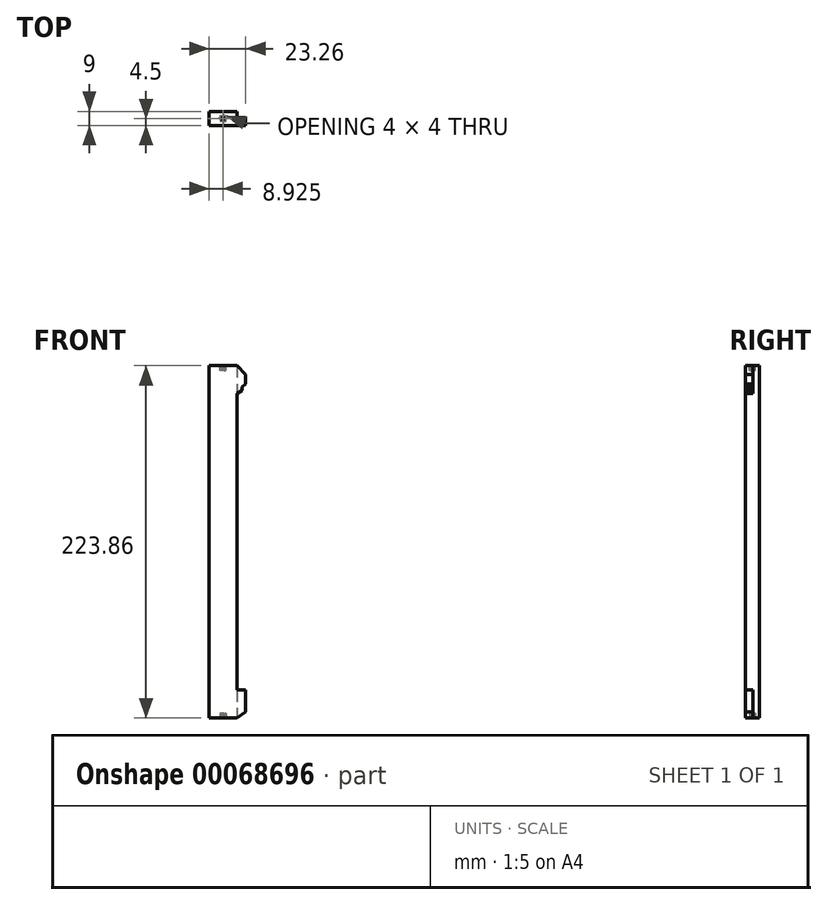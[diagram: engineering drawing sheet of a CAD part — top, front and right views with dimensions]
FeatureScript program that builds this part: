
annotation { "Feature Type Name" : "Feature", "Feature Type Description" : "" }
export const myFeature = defineFeature(function(context is Context, id is Id, definition is map)
    precondition{}
    {
        {
            var Q0;
            Q0=qCreatedBy(makeId("Front.planeOp"),FACE);
            var sketch = newSketch(context, id + "F0", { "sketchPlane" : qUnion([Q0])});
            skLineSegment(sketch, "E0", {"start": v(0, 111.93) * mm, "end": v(17.7, 111.93) * mm});
            skLineSegment(sketch, "E1", {"start": v(17.7, 111.93) * mm, "end": v(23.26, 106.39) * mm});
            skLineSegment(sketch, "E2", {"start": v(23.26, 106.39) * mm, "end": v(23.26, 100.4) * mm});
            skLineSegment(sketch, "E3", {"start": v(23.26, 100.4) * mm, "end": v(20.93, 98.25) * mm});
            skLineSegment(sketch, "E4", {"start": v(20.93, 98.25) * mm, "end": v(20.93, 96.18) * mm});
            skLineSegment(sketch, "E5", {"start": v(20.93, 96.18) * mm, "end": v(17.85, 94.28) * mm});
            skLineSegment(sketch, "E6", {"start": v(17.85, 94.28) * mm, "end": v(17.85, -94.03) * mm});
            skLineSegment(sketch, "E7", {"start": v(17.85, -94.03) * mm, "end": v(23.26, -94.03) * mm});
            skLineSegment(sketch, "E8", {"start": v(23.26, -94.03) * mm, "end": v(23.26, -107.9) * mm});
            skLineSegment(sketch, "E9", {"start": v(23.26, -107.9) * mm, "end": v(17.85, -111.93) * mm});
            skLineSegment(sketch, "E10", {"start": v(17.85, -111.93) * mm, "end": v(0, -111.93) * mm});
            skLineSegment(sketch, "E11", {"start": v(0, -111.93) * mm, "end": v(0, 111.93) * mm});
            skSolve(sketch);
        }
        {
            var Q0;
            Q0 = qSketchRegion(id + "F0", true);
            extrude(context, id + "F1", {"entities" : qUnion([Q0]), "depth" : 5 * mm});
        }
        {
            var Q0;
            Q0=makeQuery(id+"F1.opExtrude","CAP_FACE",FACE,{"disambiguationData":[OSD([sQuery(id+"F0.wireOp",EDGE,"E0"),sQuery(id+"F0.wireOp",EDGE,"E1"),sQuery(id+"F0.wireOp",EDGE,"E2"),sQuery(id+"F0.wireOp",EDGE,"E3"),sQuery(id+"F0.wireOp",EDGE,"E4"),sQuery(id+"F0.wireOp",EDGE,"E5"),sQuery(id+"F0.wireOp",EDGE,"E6"),sQuery(id+"F0.wireOp",EDGE,"E7"),sQuery(id+"F0.wireOp",EDGE,"E8"),sQuery(id+"F0.wireOp",EDGE,"E9"),sQuery(id+"F0.wireOp",EDGE,"E10"),sQuery(id+"F0.wireOp",EDGE,"E11")])],"isStart":true});
            var sketch = newSketch(context, id + "F2", { "sketchPlane" : qUnion([Q0])});
            skLineSegment(sketch, "E12.bottom", {"start": v(0, 111.93) * mm, "end": v(-17.85, 111.93) * mm});
            skLineSegment(sketch, "E12.top", {"start": v(0, -111.93) * mm, "end": v(-17.85, -111.93) * mm});
            skLineSegment(sketch, "E12.left", {"start": v(0, 111.93) * mm, "end": v(0, -111.93) * mm});
            skLineSegment(sketch, "E12.right", {"start": v(-17.85, 111.93) * mm, "end": v(-17.85, -111.93) * mm});
            skSolve(sketch);
        }
        {
            var Q0;
            Q0 = qSketchRegion(id + "F2", true);
            extrude(context, id + "F3", {"entities" : qUnion([Q0]), "operationType" : NewBodyOperationType.ADD, "depth" : 4 * mm});
        }
        {
            var Q0;
            Q0=makeQuery(id+"F3.boolean.opBoolean","MERGE",FACE,{"derivedFrom":[makeQuery(id+"F1.opExtrude","SWEPT_FACE",FACE,{"disambiguationData":[OSD([sQuery(id+"F0.wireOp",EDGE,"E0")])]}),makeQuery(id+"F3.opExtrude","SWEPT_FACE",FACE,{"disambiguationData":[OSD([sQuery(id+"F2.wireOp",EDGE,"E12.bottom")])]})]});
            var sketch = newSketch(context, id + "F4", { "sketchPlane" : qUnion([Q0])});
            skArc(sketch, "E13", {"start": v(7.51, -1) * mm, "mid": v(7.86, -1.56) * mm, "end": v(8.43, -1.91) * mm});
            skLineSegment(sketch, "E14.rect.bottom", {"start": v(10.93, 0) * mm, "end": v(10.34, 0) * mm});
            skLineSegment(sketch, "E14.rect.top", {"start": v(10.93, -1) * mm, "end": v(10.34, -1) * mm});
            skLineSegment(sketch, "E14.rect.left", {"start": v(10.93, 0) * mm, "end": v(10.93, -1) * mm});
            skLineSegment(sketch, "E14.rect.right", {"start": v(6.93, 0) * mm, "end": v(6.93, -1) * mm});
            skLineSegment(sketch, "E15.rect.bottom", {"start": v(9.43, 1.5) * mm, "end": v(8.43, 1.5) * mm});
            skLineSegment(sketch, "E15.rect.top", {"start": v(9.43, -2.5) * mm, "end": v(8.43, -2.5) * mm});
            skLineSegment(sketch, "E15.rect.left", {"start": v(9.43, 1.5) * mm, "end": v(9.43, 0.91) * mm});
            skLineSegment(sketch, "E15.rect.right", {"start": v(8.43, 1.5) * mm, "end": v(8.43, 0.91) * mm});
            skLineSegment(sketch, "E16.trimOffspring", {"start": v(7.51, 0) * mm, "end": v(6.93, 0) * mm});
            skLineSegment(sketch, "E17.trimOffspring", {"start": v(7.51, -1) * mm, "end": v(6.93, -1) * mm});
            skLineSegment(sketch, "E18.trimOffspring", {"start": v(8.43, -1.91) * mm, "end": v(8.43, -2.5) * mm});
            skLineSegment(sketch, "E19.trimOffspring", {"start": v(9.43, -1.91) * mm, "end": v(9.43, -2.5) * mm});
            skArc(sketch, "E20.trimOffspring", {"start": v(9.43, -1.91) * mm, "mid": v(9.99, -1.56) * mm, "end": v(10.34, -1) * mm});
            skArc(sketch, "E21.trimOffspring", {"start": v(10.34, 0) * mm, "mid": v(9.99, 0.56) * mm, "end": v(9.43, 0.91) * mm});
            skArc(sketch, "E22.trimOffspring", {"start": v(8.43, 0.91) * mm, "mid": v(7.86, 0.56) * mm, "end": v(7.51, 0) * mm});
            skSolve(sketch);
        }
        {
            var Q0;
            Q0 = qSketchRegion(id + "F4", true);
            extrude(context, id + "F5", {"entities" : qUnion([Q0]), "oppositeDirection" : true, "depth" : 3 * mm});
        }
        {
            var Q0;
            Q0=makeQuery(id+"F5.opExtrude","SWEPT_BODY",BODY,{"disambiguationData":[OSD([sQuery(id+"F4.wireOp",EDGE,"E13"),sQuery(id+"F4.wireOp",EDGE,"E14.rect.bottom"),sQuery(id+"F4.wireOp",EDGE,"E14.rect.top"),sQuery(id+"F4.wireOp",EDGE,"E14.rect.left"),sQuery(id+"F4.wireOp",EDGE,"E14.rect.right"),sQuery(id+"F4.wireOp",EDGE,"E15.rect.bottom"),sQuery(id+"F4.wireOp",EDGE,"E15.rect.top"),sQuery(id+"F4.wireOp",EDGE,"E15.rect.left"),sQuery(id+"F4.wireOp",EDGE,"E15.rect.right"),sQuery(id+"F4.wireOp",EDGE,"E16.trimOffspring"),sQuery(id+"F4.wireOp",EDGE,"E17.trimOffspring"),sQuery(id+"F4.wireOp",EDGE,"E18.trimOffspring"),sQuery(id+"F4.wireOp",EDGE,"E19.trimOffspring"),sQuery(id+"F4.wireOp",EDGE,"E20.trimOffspring"),sQuery(id+"F4.wireOp",EDGE,"E21.trimOffspring"),sQuery(id+"F4.wireOp",EDGE,"E22.trimOffspring")])]});
            var Q1;
            Q1=qCreatedBy(makeId("Top.planeOp"),FACE);
            mirror(context, id + "F6", {"entities" : qUnion([Q0]), "mirrorPlane" : qUnion([Q1])});
        }
        {
            var Q0;
            Q0=makeQuery(id+"F5.opExtrude","SWEPT_BODY",BODY,{"disambiguationData":[OSD([sQuery(id+"F4.wireOp",EDGE,"E13"),sQuery(id+"F4.wireOp",EDGE,"E14.rect.bottom"),sQuery(id+"F4.wireOp",EDGE,"E14.rect.top"),sQuery(id+"F4.wireOp",EDGE,"E14.rect.left"),sQuery(id+"F4.wireOp",EDGE,"E14.rect.right"),sQuery(id+"F4.wireOp",EDGE,"E15.rect.bottom"),sQuery(id+"F4.wireOp",EDGE,"E15.rect.top"),sQuery(id+"F4.wireOp",EDGE,"E15.rect.left"),sQuery(id+"F4.wireOp",EDGE,"E15.rect.right"),sQuery(id+"F4.wireOp",EDGE,"E16.trimOffspring"),sQuery(id+"F4.wireOp",EDGE,"E17.trimOffspring"),sQuery(id+"F4.wireOp",EDGE,"E18.trimOffspring"),sQuery(id+"F4.wireOp",EDGE,"E19.trimOffspring"),sQuery(id+"F4.wireOp",EDGE,"E20.trimOffspring"),sQuery(id+"F4.wireOp",EDGE,"E21.trimOffspring"),sQuery(id+"F4.wireOp",EDGE,"E22.trimOffspring")])]});
            var Q1;
            Q1=makeQuery(id+"F1.opExtrude","SWEPT_BODY",BODY,{"disambiguationData":[OSD([sQuery(id+"F0.wireOp",EDGE,"E0"),sQuery(id+"F0.wireOp",EDGE,"E1"),sQuery(id+"F0.wireOp",EDGE,"E2"),sQuery(id+"F0.wireOp",EDGE,"E3"),sQuery(id+"F0.wireOp",EDGE,"E4"),sQuery(id+"F0.wireOp",EDGE,"E5"),sQuery(id+"F0.wireOp",EDGE,"E6"),sQuery(id+"F0.wireOp",EDGE,"E7"),sQuery(id+"F0.wireOp",EDGE,"E8"),sQuery(id+"F0.wireOp",EDGE,"E9"),sQuery(id+"F0.wireOp",EDGE,"E10"),sQuery(id+"F0.wireOp",EDGE,"E11")])]});
            booleanBodies(context, id + "F7", {"operationType" : BooleanOperationType.SUBTRACTION, "tools" : qUnion([Q0]), "targets" : qUnion([Q1])});
        }
        {
            var Q0;
            Q0=makeQuery(id+"F6.opPattern","COPY",BODY,{"derivedFrom":makeQuery(id+"F5.opExtrude","SWEPT_BODY",BODY,{"disambiguationData":[OSD([sQuery(id+"F4.wireOp",EDGE,"E13"),sQuery(id+"F4.wireOp",EDGE,"E14.rect.bottom"),sQuery(id+"F4.wireOp",EDGE,"E14.rect.top"),sQuery(id+"F4.wireOp",EDGE,"E14.rect.left"),sQuery(id+"F4.wireOp",EDGE,"E14.rect.right"),sQuery(id+"F4.wireOp",EDGE,"E15.rect.bottom"),sQuery(id+"F4.wireOp",EDGE,"E15.rect.top"),sQuery(id+"F4.wireOp",EDGE,"E15.rect.left"),sQuery(id+"F4.wireOp",EDGE,"E15.rect.right"),sQuery(id+"F4.wireOp",EDGE,"E16.trimOffspring"),sQuery(id+"F4.wireOp",EDGE,"E17.trimOffspring"),sQuery(id+"F4.wireOp",EDGE,"E18.trimOffspring"),sQuery(id+"F4.wireOp",EDGE,"E19.trimOffspring"),sQuery(id+"F4.wireOp",EDGE,"E20.trimOffspring"),sQuery(id+"F4.wireOp",EDGE,"E21.trimOffspring"),sQuery(id+"F4.wireOp",EDGE,"E22.trimOffspring")])]}),"instanceName":"1"});
            var Q1;
            Q1=makeQuery(id+"F1.opExtrude","SWEPT_BODY",BODY,{"disambiguationData":[OSD([sQuery(id+"F0.wireOp",EDGE,"E0"),sQuery(id+"F0.wireOp",EDGE,"E1"),sQuery(id+"F0.wireOp",EDGE,"E2"),sQuery(id+"F0.wireOp",EDGE,"E3"),sQuery(id+"F0.wireOp",EDGE,"E4"),sQuery(id+"F0.wireOp",EDGE,"E5"),sQuery(id+"F0.wireOp",EDGE,"E6"),sQuery(id+"F0.wireOp",EDGE,"E7"),sQuery(id+"F0.wireOp",EDGE,"E8"),sQuery(id+"F0.wireOp",EDGE,"E9"),sQuery(id+"F0.wireOp",EDGE,"E10"),sQuery(id+"F0.wireOp",EDGE,"E11")])]});
            booleanBodies(context, id + "F8", {"operationType" : BooleanOperationType.SUBTRACTION, "tools" : qUnion([Q0]), "targets" : qUnion([Q1])});
        }
    });
